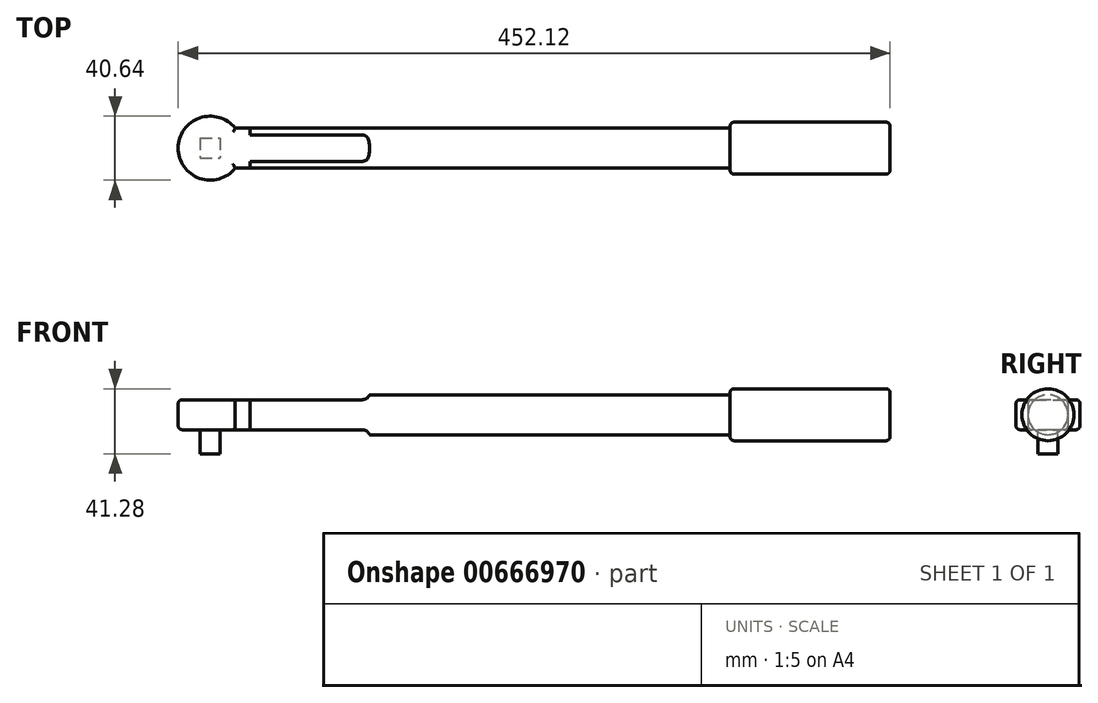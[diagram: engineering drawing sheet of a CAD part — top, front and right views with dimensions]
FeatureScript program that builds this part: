
annotation { "Feature Type Name" : "Feature", "Feature Type Description" : "" }
export const myFeature = defineFeature(function(context is Context, id is Id, definition is map)
    precondition{}
    {
        {
            var Q0;
            Q0=qCreatedBy(makeId("Right.planeOp"),FACE);
            var sketch = newSketch(context, id + "F0", { "sketchPlane" : qUnion([Q0])});
            skCircle(sketch, "E0", {"center": v(0, 0) * mm, "radius": 12.7 * mm});
            skSolve(sketch);
        }
        {
            var Q0;
            Q0 = qSketchRegion(id + "F0", true);
            extrude(context, id + "F1", {"entities" : qUnion([Q0]), "depth" : 406.4 * mm, "offsetDistance" : 25.4 * mm});
        }
        {
            var Q0;
            Q0=makeQuery(id+"F1.opExtrude","CAP_FACE",FACE,{"disambiguationData":[OSD([sQuery(id+"F0.wireOp",EDGE,"E0")])],"isStart":false});
            var sketch = newSketch(context, id + "F2", { "sketchPlane" : qUnion([Q0])});
            skCircle(sketch, "E1", {"center": v(0, 0) * mm, "radius": 16.51 * mm});
            skSolve(sketch);
        }
        {
            var Q0;
            Q0 = qSketchRegion(id + "F2", true);
            extrude(context, id + "F3", {"entities" : qUnion([Q0]), "operationType" : NewBodyOperationType.ADD, "oppositeDirection" : true, "depth" : 101.6 * mm, "offsetDistance" : 25.4 * mm});
        }
        {
            var Q0;
            Q0=qCreatedBy(makeId("Top.planeOp"),FACE);
            var sketch = newSketch(context, id + "F4", { "sketchPlane" : qUnion([Q0])});
            skArc(sketch, "E2", {"start": v(-9.54, 12.7) * mm, "mid": v(-45.72, 0) * mm, "end": v(-9.54, -12.7) * mm});
            skLineSegment(sketch, "E3.bottom", {"start": v(0, 12.7) * mm, "end": v(-9.54, 12.7) * mm});
            skLineSegment(sketch, "E3.top", {"start": v(0, -12.7) * mm, "end": v(-9.54, -12.7) * mm});
            skLineSegment(sketch, "E3.left", {"start": v(0, 12.7) * mm, "end": v(0, -12.7) * mm});
            skSolve(sketch);
        }
        {
            var Q0;
            Q0 = qSketchRegion(id + "F4", true);
            extrude(context, id + "F5", {"entities" : qUnion([Q0]), "operationType" : NewBodyOperationType.ADD, "endBound" : BoundingType.SYMMETRIC, "depth" : 19.05 * mm, "offsetDistance" : 25.4 * mm});
        }
        {
            var Q0;
            Q0=qCreatedBy(makeId("Front.planeOp"),FACE);
            var sketch = newSketch(context, id + "F6", { "sketchPlane" : qUnion([Q0])});
            skLineSegment(sketch, "E4.bottom", {"start": v(0, 9.52) * mm, "end": v(76.2, 9.52) * mm});
            skLineSegment(sketch, "E4.top", {"start": v(0, 12.7) * mm, "end": v(76.2, 12.7) * mm});
            skLineSegment(sketch, "E4.left", {"start": v(0, 9.52) * mm, "end": v(0, 12.7) * mm});
            skLineSegment(sketch, "E4.right", {"start": v(76.2, 9.52) * mm, "end": v(76.2, 12.7) * mm});
            skLineSegment(sketch, "E5.bottom", {"start": v(0, -9.53) * mm, "end": v(76.2, -9.53) * mm});
            skLineSegment(sketch, "E5.top", {"start": v(0, -12.7) * mm, "end": v(76.2, -12.7) * mm});
            skLineSegment(sketch, "E5.left", {"start": v(0, -9.53) * mm, "end": v(0, -12.7) * mm});
            skLineSegment(sketch, "E5.right", {"start": v(76.2, -9.53) * mm, "end": v(76.2, -12.7) * mm});
            skSolve(sketch);
        }
        {
            var Q0;
            Q0 = qSketchRegion(id + "F6", true);
            extrude(context, id + "F7", {"entities" : qUnion([Q0]), "operationType" : NewBodyOperationType.REMOVE, "endBound" : BoundingType.SYMMETRIC, "depth" : 25.4 * mm, "offsetDistance" : 25.4 * mm});
        }
        {
            var Q0;
            Q0=makeQuery(id+"F7.boolean.opBoolean","COPY",EDGE,{"derivedFrom":makeQuery(id+"F7.opExtrude","SWEPT_EDGE",EDGE,{"disambiguationData":[OSD([sQuery(id+"F6.wireOp",EDGE,"E4.bottom"),sQuery(id+"F6.wireOp",EDGE,"E4.right")])]})});
            fillet(context, id + "F8", {"entities" : qUnion([Q0]), "radius" : 5.08 * mm, "tangentPropagation" : true, "allowEdgeOverflow" : false});
        }
        {
            var Q0;
            Q0=makeQuery(id+"F7.boolean.opBoolean","COPY",EDGE,{"derivedFrom":makeQuery(id+"F7.opExtrude","SWEPT_EDGE",EDGE,{"disambiguationData":[OSD([sQuery(id+"F6.wireOp",EDGE,"E5.bottom"),sQuery(id+"F6.wireOp",EDGE,"E5.right")])]})});
            fillet(context, id + "F9", {"entities" : qUnion([Q0]), "radius" : 5.08 * mm, "tangentPropagation" : true, "allowEdgeOverflow" : false});
        }
        {
            var Q0;
            Q0=makeQuery(id+"F5.opExtrude","CAP_EDGE",EDGE,{"disambiguationData":[OSD([sQuery(id+"F4.wireOp",EDGE,"E2")])],"isStart":true});
            var Q1;
            Q1=makeQuery(id+"F5.opExtrude","CAP_EDGE",EDGE,{"disambiguationData":[OSD([sQuery(id+"F4.wireOp",EDGE,"E2")])],"isStart":false});
            var Q2;
            Q2=makeQuery(id+"F5.opExtrude","CAP_EDGE",EDGE,{"disambiguationData":[OSD([sQuery(id+"F4.wireOp",EDGE,"E3.top")])],"isStart":true});
            var Q3;
            Q3=makeQuery(id+"F5.opExtrude","CAP_EDGE",EDGE,{"disambiguationData":[OSD([sQuery(id+"F4.wireOp",EDGE,"E3.top")])],"isStart":false});
            var Q4;
            Q4=makeQuery(id+"F5.opExtrude","CAP_EDGE",EDGE,{"disambiguationData":[OSD([sQuery(id+"F4.wireOp",EDGE,"E3.bottom")])],"isStart":true});
            var Q5;
            Q5=makeQuery(id+"F5.opExtrude","CAP_EDGE",EDGE,{"disambiguationData":[OSD([sQuery(id+"F4.wireOp",EDGE,"E3.bottom")])],"isStart":false});
            var Q6;
            Q6=makeQuery(id+"F3.opExtrude","CAP_EDGE",EDGE,{"disambiguationData":[OSD([sQuery(id+"F2.wireOp",EDGE,"E1")])],"isStart":true});
            var Q7;
            Q7=makeQuery(id+"F3.opExtrude","CAP_EDGE",EDGE,{"disambiguationData":[OSD([sQuery(id+"F2.wireOp",EDGE,"E1")])],"isStart":false});
            fillet(context, id + "F10", {"entities" : qUnion([Q0, Q1, Q2, Q3, Q4, Q5, Q6, Q7]), "radius" : 2.54 * mm, "tangentPropagation" : true, "allowEdgeOverflow" : false});
        }
        {
            var Q0;
            Q0=makeQuery(id+"F7.boolean.opBoolean","MERGE",FACE,{"derivedFrom":[makeQuery(id+"F5.opExtrude","CAP_FACE",FACE,{"disambiguationData":[OSD([sQuery(id+"F4.wireOp",EDGE,"E2"),sQuery(id+"F4.wireOp",EDGE,"E3.bottom"),sQuery(id+"F4.wireOp",EDGE,"E3.top"),sQuery(id+"F4.wireOp",EDGE,"E3.left")])],"isStart":true}),makeQuery(id+"F7.opExtrude","SWEPT_FACE",FACE,{"disambiguationData":[OSD([sQuery(id+"F6.wireOp",EDGE,"E5.bottom")])]})]});
            var sketch = newSketch(context, id + "F11", { "sketchPlane" : qUnion([Q0])});
            skLineSegment(sketch, "E6.bottom", {"start": v(-31.75, -6.35) * mm, "end": v(-19.05, -6.35) * mm});
            skLineSegment(sketch, "E6.top", {"start": v(-31.75, 6.35) * mm, "end": v(-19.05, 6.35) * mm});
            skLineSegment(sketch, "E6.left", {"start": v(-31.75, -6.35) * mm, "end": v(-31.75, 6.35) * mm});
            skLineSegment(sketch, "E6.right", {"start": v(-19.05, -6.35) * mm, "end": v(-19.05, 6.35) * mm});
            skSolve(sketch);
        }
        {
            var Q0;
            Q0 = qSketchRegion(id + "F11", true);
            extrude(context, id + "F12", {"entities" : qUnion([Q0]), "operationType" : NewBodyOperationType.ADD, "depth" : 15.24 * mm, "offsetDistance" : 25.4 * mm});
        }
    });
